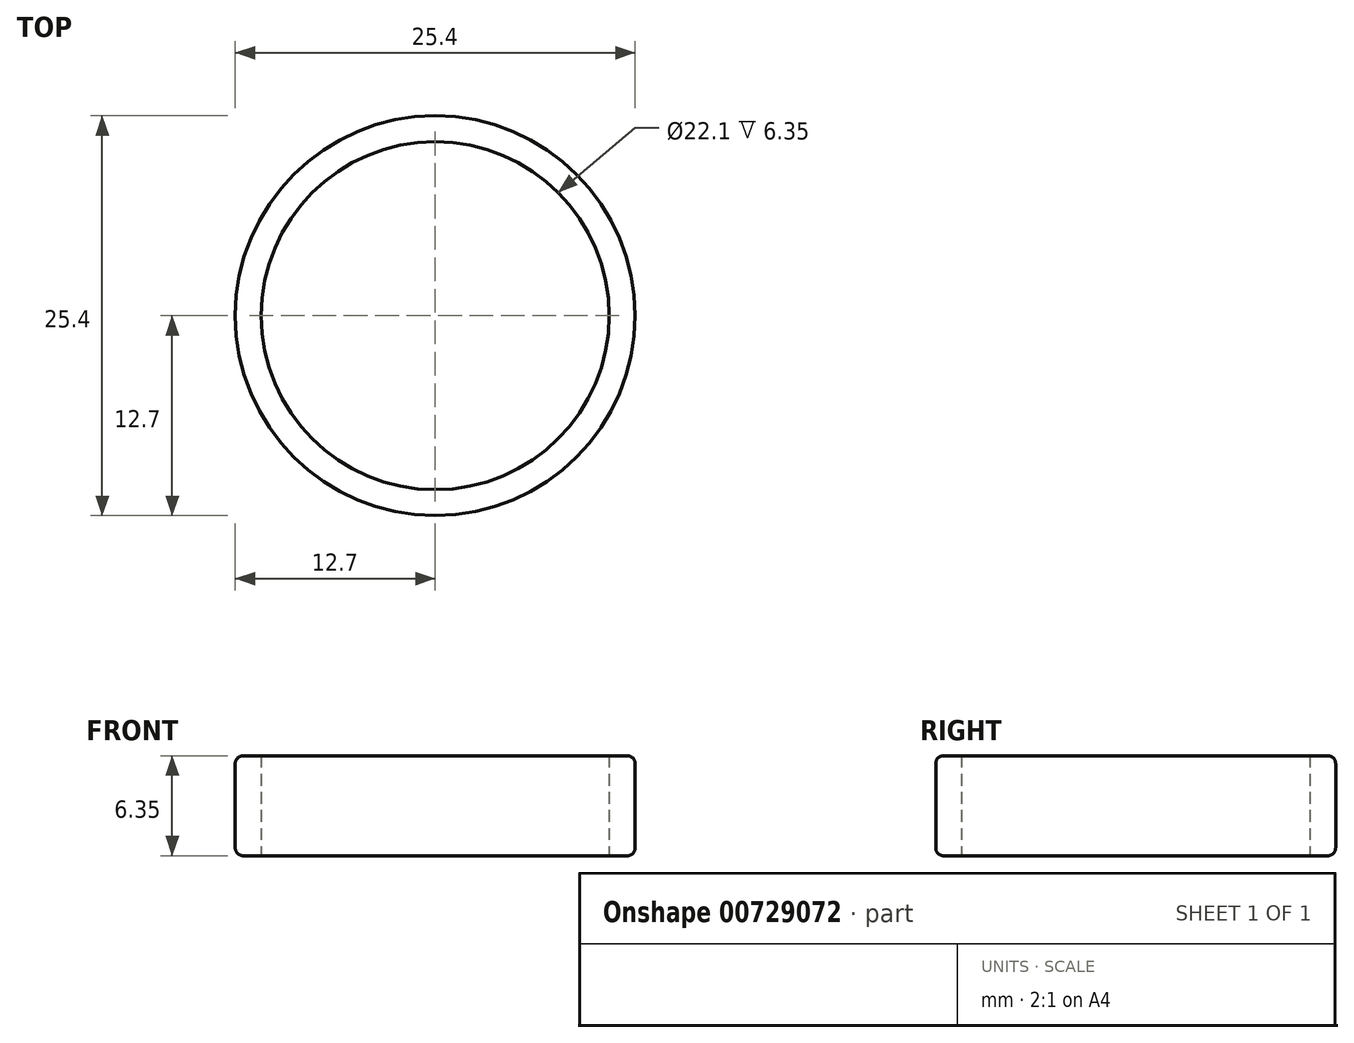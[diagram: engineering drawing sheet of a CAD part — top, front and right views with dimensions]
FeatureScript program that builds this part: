
annotation { "Feature Type Name" : "Feature", "Feature Type Description" : "" }
export const myFeature = defineFeature(function(context is Context, id is Id, definition is map)
    precondition{}
    {
        {
            var Q0;
            Q0=qCreatedBy(makeId("Front.planeOp"),FACE);
            var sketch = newSketch(context, id + "F0", { "sketchPlane" : qUnion([Q0])});
            skLineSegment(sketch, "E0.left", {"start": v(0, 0) * mm, "end": v(0, 6.35) * mm});
            skLineSegment(sketch, "E1.top", {"start": v(-2.02, 20) * mm, "end": v(-3.32, 20) * mm});
            skLineSegment(sketch, "E1.right", {"start": v(-3.82, 5.7) * mm, "end": v(-3.82, 19.5) * mm});
            skLineSegment(sketch, "E2", {"start": v(-6.61, 1.5) * mm, "end": v(-7.17, 1.5) * mm});
            skLineSegment(sketch, "E3", {"start": v(-9.4, 5.85) * mm, "end": v(-9.4, 3.93) * mm});
            skPoint(sketch, "E4.orphan", {"position": v(-12.7, 1.5) * mm});
            skPoint(sketch, "E5.end.orphan", {"position": v(-6.35, 0) * mm});
            skPoint(sketch, "E5.start.orphan", {"position": v(-6.35, 1.5) * mm});
            skPoint(sketch, "E6.orphan", {"position": v(0, 1.5) * mm});
            skArc(sketch, "E7", {"start": v(-9.4, 3.93) * mm, "mid": v(-8.54, 2.1) * mm, "end": v(-6.61, 1.5) * mm});
            skArc(sketch, "E8", {"start": v(-3.82, 5.7) * mm, "mid": v(-3.81, 6.02) * mm, "end": v(-3.82, 6.35) * mm});
            skPoint(sketch, "E9.orphan", {"position": v(-3.82, 1.5) * mm});
            skPoint(sketch, "E10.orphan", {"position": v(-9.4, 1.5) * mm});
            skLineSegment(sketch, "E11.top", {"start": v(0, 4.66) * mm, "end": v(-1.52, 4.66) * mm});
            skLineSegment(sketch, "E11.left", {"start": v(0, 6.35) * mm, "end": v(0, 4.66) * mm});
            skLineSegment(sketch, "E11.right", {"start": v(-2.02, 20) * mm, "end": v(-2.02, 5.16) * mm});
            skPoint(sketch, "E12.visualSharp", {"position": v(-12.7, 0) * mm});
            skPoint(sketch, "E13.visualSharp", {"position": v(-3.82, 20) * mm});
            skArc(sketch, "E13.filletArc", {"start": v(-3.32, 20) * mm, "mid": v(-3.68, 19.85) * mm, "end": v(-3.82, 19.5) * mm});
            skPoint(sketch, "E14.visualSharp", {"position": v(-12.7, 6.35) * mm});
            skPoint(sketch, "E15.visualSharp", {"position": v(-9.4, 6.35) * mm});
            skArc(sketch, "E15.filletArc", {"start": v(-9.4, 5.85) * mm, "mid": v(-9.55, 6.2) * mm, "end": v(-9.9, 6.35) * mm});
            skPoint(sketch, "E16.visualSharp", {"position": v(-2.02, 4.66) * mm});
            skArc(sketch, "E16.filletArc", {"start": v(-2.02, 5.16) * mm, "mid": v(-1.87, 4.8) * mm, "end": v(-1.52, 4.66) * mm});
            skArc(sketch, "E17", {"start": v(0, -0.12) * mm, "mid": v(-1.3, -0.8) * mm, "end": v(-1.5, -2.23) * mm});
            skLineSegment(sketch, "E18", {"start": v(0, 0) * mm, "end": v(0, -0.12) * mm});
            skLineSegment(sketch, "E19", {"start": v(-3.82, 5.7) * mm, "end": v(-3.82, 3.93) * mm});
            skArc(sketch, "E20", {"start": v(-6.61, 1.5) * mm, "mid": v(-4.76, 2.2) * mm, "end": v(-3.82, 3.93) * mm});
            skArc(sketch, "E21", {"start": v(-1.5, -2.23) * mm, "mid": v(-3.68, -0.58) * mm, "end": v(-6.35, 0) * mm});
            skPoint(sketch, "E22", {"position": v(-3.82, 12.6) * mm});
            skLineSegment(sketch, "E23", {"start": v(-11.05, 6.35) * mm, "end": v(-11.05, 0) * mm});
            skPoint(sketch, "E23.endSnap0", {"position": v(-11.05, 6.35) * mm});
            skPoint(sketch, "E24.orphan", {"position": v(-12.2, 6.35) * mm});
            skLineSegment(sketch, "E25.bottom", {"start": v(-11.05, 6.35) * mm, "end": v(-12.7, 6.35) * mm});
            skLineSegment(sketch, "E25.top", {"start": v(-11.05, 0) * mm, "end": v(-12.7, 0) * mm});
            skLineSegment(sketch, "E25.right", {"start": v(-12.7, 6.35) * mm, "end": v(-12.7, 0) * mm});
            skSolve(sketch);
        }
        {
            var Q0;
            Q0=makeQuery(id+"F0.imprint","IMPRINT",FACE,{"disambiguationData":[TD([[makeQuery(id+"F0.imprint","IMPRINT",EDGE,{"derivedFrom":sQuery(id+"F0.wireOp",EDGE,"E25.bottom")}),1.0]])]});
            var Q1;
            Q1=sQuery(id+"F0.wireOp",EDGE,"E0.left");
            revolve(context, id + "F1", {"surfaceOperationType" : NewSurfaceOperationType.NEW, "entities" : qUnion([Q0]), "axis" : qUnion([Q1]), "revolveType" : RevolveType.FULL});
        }
        {
            var Q0;
            Q0=makeQuery(id+"F1.opRevolve","SWEPT_EDGE",EDGE,{"disambiguationData":[OSD([sQuery(id+"F0.wireOp",EDGE,"E25.bottom"),sQuery(id+"F0.wireOp",EDGE,"E25.right")])]});
            var Q1;
            Q1=makeQuery(id+"F1.opRevolve","SWEPT_EDGE",EDGE,{"disambiguationData":[OSD([sQuery(id+"F0.wireOp",EDGE,"E25.top"),sQuery(id+"F0.wireOp",EDGE,"E25.right")])]});
            fillet(context, id + "F2", {"entities" : qUnion([Q0, Q1]), "radius" : 0.5 * mm, "tangentPropagation" : true, "allowEdgeOverflow" : false});
        }
    });
